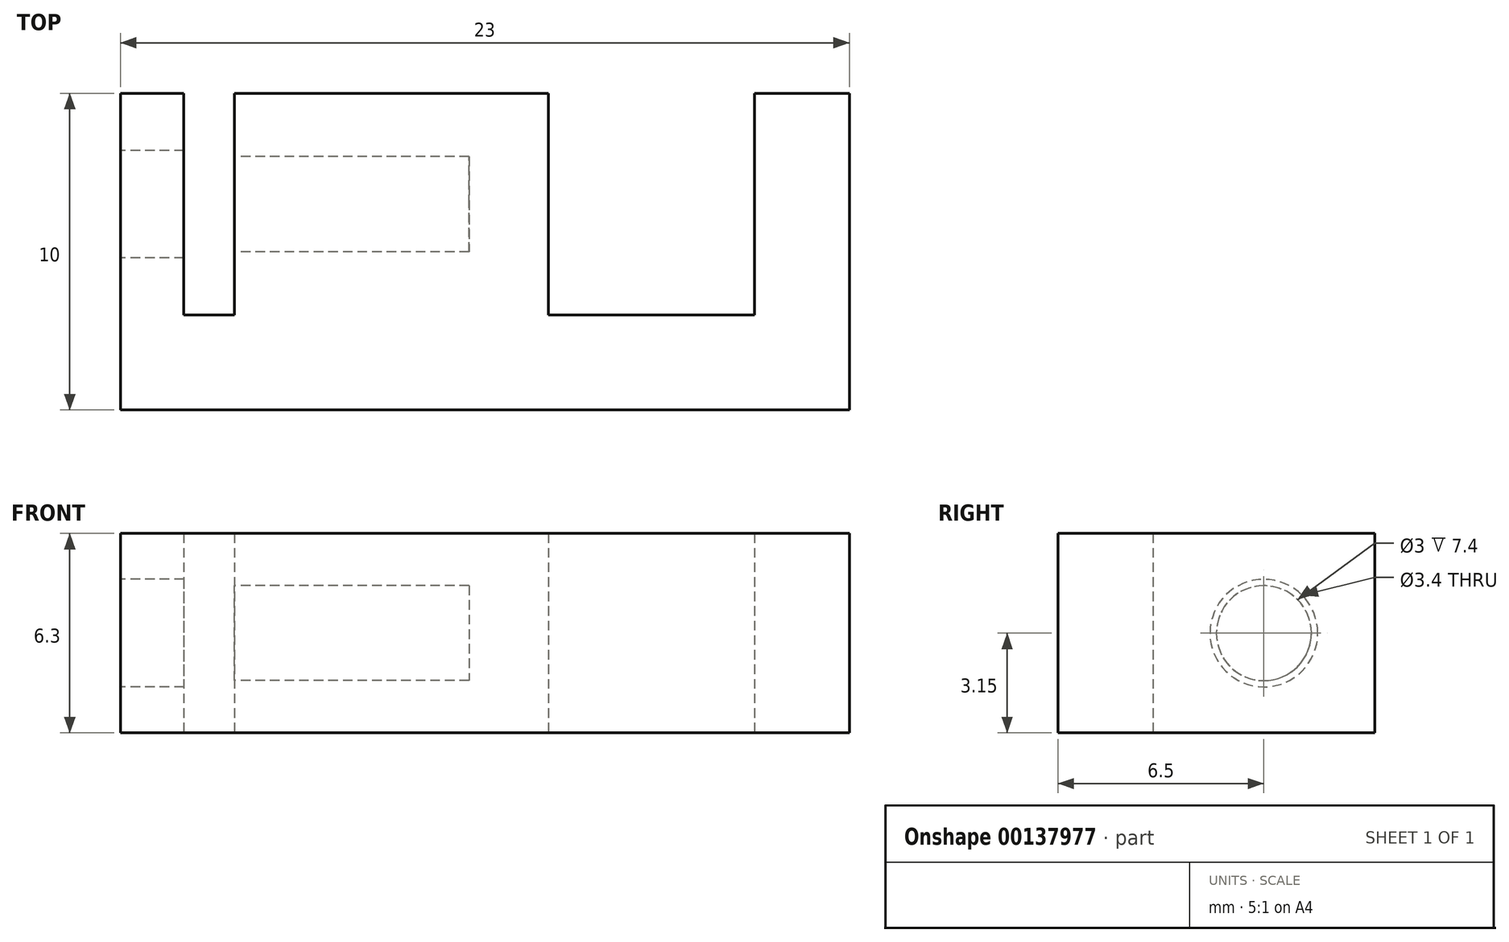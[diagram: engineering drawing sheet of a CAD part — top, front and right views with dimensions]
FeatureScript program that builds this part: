
annotation { "Feature Type Name" : "Feature", "Feature Type Description" : "" }
export const myFeature = defineFeature(function(context is Context, id is Id, definition is map)
    precondition{}
    {
        {
            var Q0;
            Q0=qCreatedBy(makeId("Top.planeOp"),FACE);
            var sketch = newSketch(context, id + "F0", { "sketchPlane" : qUnion([Q0])});
            skLineSegment(sketch, "E0", {"start": v(-11.5, 5) * mm, "end": v(-11.5, -5) * mm});
            skLineSegment(sketch, "E1", {"start": v(-11.5, -5) * mm, "end": v(11.5, -5) * mm});
            skLineSegment(sketch, "E2", {"start": v(11.5, -5) * mm, "end": v(11.5, 5) * mm});
            skLineSegment(sketch, "E3", {"start": v(11.5, 5) * mm, "end": v(8.5, 5) * mm});
            skLineSegment(sketch, "E4", {"start": v(8.5, 5) * mm, "end": v(8.5, -2) * mm});
            skLineSegment(sketch, "E5", {"start": v(8.5, -2) * mm, "end": v(2, -2) * mm});
            skLineSegment(sketch, "E6", {"start": v(2, -2) * mm, "end": v(2, 5) * mm});
            skLineSegment(sketch, "E7", {"start": v(2, 5) * mm, "end": v(-7.9, 5) * mm});
            skLineSegment(sketch, "E8", {"start": v(-7.9, 5) * mm, "end": v(-7.9, -2) * mm});
            skLineSegment(sketch, "E9", {"start": v(-7.9, -2) * mm, "end": v(-9.5, -2) * mm});
            skLineSegment(sketch, "E10", {"start": v(-9.5, -2) * mm, "end": v(-9.5, 5) * mm});
            skLineSegment(sketch, "E11", {"start": v(-9.5, 5) * mm, "end": v(-11.5, 5) * mm});
            skPoint(sketch, "E12", {"position": v(-11.5, 0) * mm});
            skPoint(sketch, "E13", {"position": v(0, -5) * mm});
            skSolve(sketch);
        }
        {
            var Q0;
            Q0=qSketchRegion(id+"F0",true);
            extrude(context, id + "F1", {"entities" : qUnion([Q0]), "depth" : 6.3 * mm, "symmetric" : true});
        }
        {
            var Q0;
            Q0=makeQuery(id+"F1.opExtrude","SWEPT_FACE",FACE,{"disambiguationData":[OSD([sQuery(id+"F0.wireOp",EDGE,"E0")])]});
            var sketch = newSketch(context, id + "F2", { "sketchPlane" : qUnion([Q0])});
            skCircle(sketch, "E14", {"center": v(-1.5, 0) * mm, "radius": 1.5 * mm});
            skCircle(sketch, "E15.0", {"center": v(-1.5, 0) * mm, "radius": 1.7 * mm});
            skSolve(sketch);
        }
        {
            var Q0;
            Q0=makeQuery(id+"F2.imprint","IMPRINT",FACE,{"disambiguationData":[TD([[makeQuery(id+"F2.imprint","IMPRINT",EDGE,{"derivedFrom":sQuery(id+"F2.wireOp",EDGE,"E14")}),1.0]])]});
            extrude(context, id + "F3", {"entities" : qUnion([Q0]), "operationType" : NewBodyOperationType.REMOVE, "oppositeDirection" : true, "depth" : 11 * mm});
        }
        {
            var Q0;
            Q0=makeQuery(id+"F2.imprint","IMPRINT",FACE,{"disambiguationData":[TD([[makeQuery(id+"F2.imprint","IMPRINT",EDGE,{"derivedFrom":sQuery(id+"F2.wireOp",EDGE,"E14")}),-1.0]])]});
            extrude(context, id + "F4", {"entities" : qUnion([Q0]), "operationType" : NewBodyOperationType.REMOVE, "endBound" : BoundingType.UP_TO_NEXT, "oppositeDirection" : true, "depth" : 25 * mm});
        }
    });
